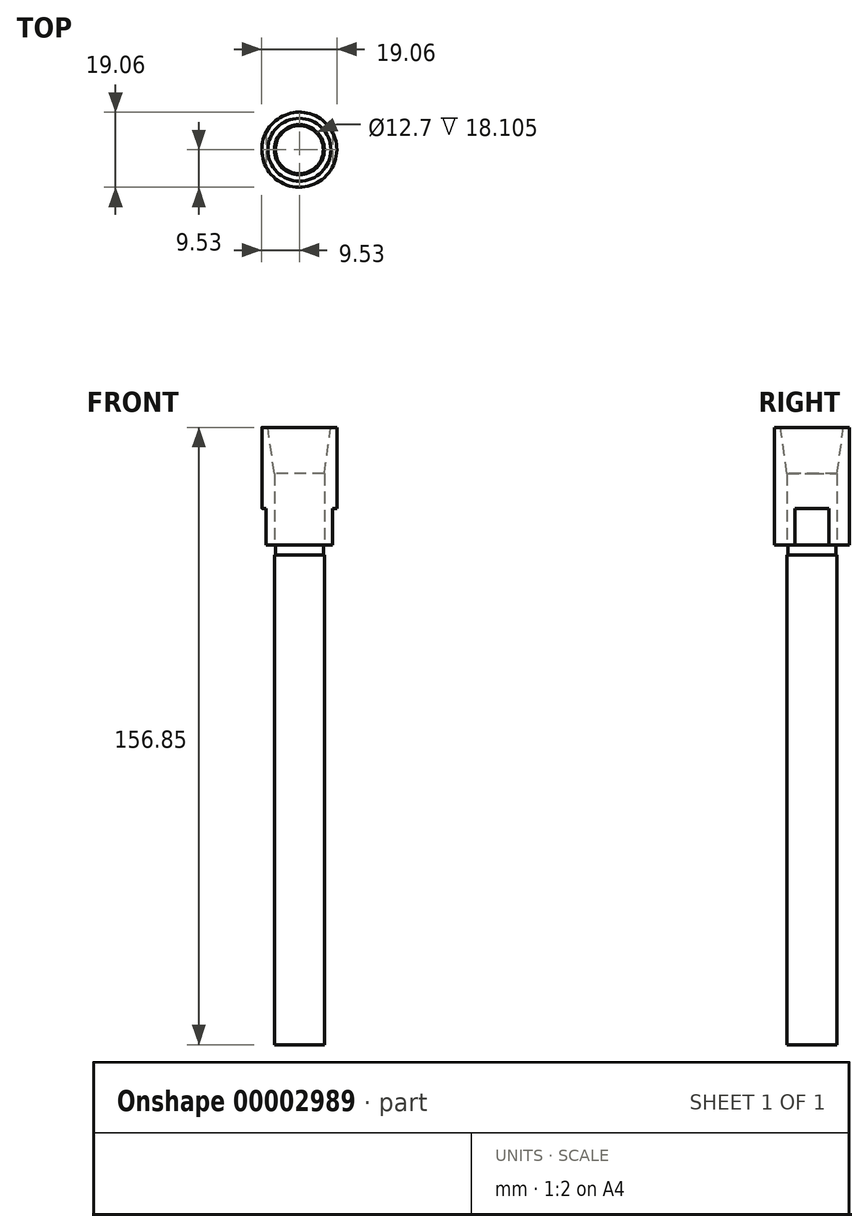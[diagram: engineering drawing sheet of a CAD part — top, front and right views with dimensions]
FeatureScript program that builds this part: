
annotation { "Feature Type Name" : "Feature", "Feature Type Description" : "" }
export const myFeature = defineFeature(function(context is Context, id is Id, definition is map)
    precondition{}
    {
        {
            var Q0;
            Q0=qCreatedBy(makeId("Top.planeOp"),FACE);
            var sketch = newSketch(context, id + "F0", { "sketchPlane" : qUnion([Q0])});
            skCircle(sketch, "E0", {"center": v(0, 0) * mm, "radius": 6.35 * mm});
            skCircle(sketch, "E1", {"center": v(0, 0) * mm, "radius": 9.53 * mm});
            skCircle(sketch, "E2", {"center": v(0, 0) * mm, "radius": 6.1 * mm});
            skSolve(sketch);
        }
        {
            var Q0;
            Q0=makeQuery(id+"F0.imprint","IMPRINT",FACE,{"disambiguationData":[TD([[makeQuery(id+"F0.imprint","IMPRINT",EDGE,{"derivedFrom":sQuery(id+"F0.wireOp",EDGE,"E0")}),1.0]])]});
            var Q1;
            Q1=makeQuery(id+"F0.imprint","IMPRINT",FACE,{"disambiguationData":[TD([[makeQuery(id+"F0.imprint","IMPRINT",EDGE,{"derivedFrom":sQuery(id+"F0.wireOp",EDGE,"E2")}),1.0]])]});
            extrude(context, id + "F1", {"entities" : qUnion([Q0, Q1]), "oppositeDirection" : true, "depth" : 127 * mm});
        }
        {
            var Q0;
            Q0=makeQuery(id+"F0.imprint","IMPRINT",FACE,{"disambiguationData":[TD([[makeQuery(id+"F0.imprint","IMPRINT",EDGE,{"derivedFrom":sQuery(id+"F0.wireOp",EDGE,"E0")}),1.0]])]});
            extrude(context, id + "F2", {"entities" : qUnion([Q0]), "operationType" : NewBodyOperationType.REMOVE, "oppositeDirection" : true, "depth" : 2.54 * mm});
        }
        {
            var Q0;
            Q0=makeQuery(id+"F0.imprint","IMPRINT",FACE,{"disambiguationData":[TD([[makeQuery(id+"F0.imprint","IMPRINT",EDGE,{"derivedFrom":sQuery(id+"F0.wireOp",EDGE,"E0")}),-1.0]])]});
            extrude(context, id + "F3", {"entities" : qUnion([Q0]), "depth" : 29.84 * mm});
        }
        {
            var Q0;
            Q0=qCreatedBy(makeId("Front.planeOp"),FACE);
            var sketch = newSketch(context, id + "F4", { "sketchPlane" : qUnion([Q0])});
            skLineSegment(sketch, "E3", {"start": v(-9.53, 0) * mm, "end": v(-9.53, 10.73) * mm, "construction": true});
            skLineSegment(sketch, "E4", {"start": v(9.53, 0) * mm, "end": v(9.53, 10.31) * mm, "construction": true});
            skLineSegment(sketch, "E5.rect.bottom", {"start": v(-10.55, 0) * mm, "end": v(-8.5, 0) * mm});
            skLineSegment(sketch, "E5.rect.top", {"start": v(-10.55, 9.27) * mm, "end": v(-8.5, 9.27) * mm});
            skLineSegment(sketch, "E5.rect.left", {"start": v(-10.55, 0) * mm, "end": v(-10.55, 9.27) * mm});
            skLineSegment(sketch, "E5.rect.right", {"start": v(-8.5, 0) * mm, "end": v(-8.5, 9.27) * mm});
            skPoint(sketch, "E5.rect.middle", {"position": v(-9.53, 4.64) * mm});
            skLineSegment(sketch, "E6", {"start": v(0, 0) * mm, "end": v(0, 9.93) * mm, "construction": true});
            skLineSegment(sketch, "E7.0.MirrorCS", {"start": v(10.55, 9.27) * mm, "end": v(8.5, 9.27) * mm});
            skLineSegment(sketch, "E8.0.MirrorCS", {"start": v(8.5, 0) * mm, "end": v(8.5, 9.27) * mm});
            skLineSegment(sketch, "E9.0.MirrorCS", {"start": v(10.55, 0) * mm, "end": v(8.5, 0) * mm});
            skLineSegment(sketch, "E10.0.MirrorCS", {"start": v(10.55, 0) * mm, "end": v(10.55, 9.27) * mm});
            skSolve(sketch);
        }
        {
            var Q0;
            Q0 = qSketchRegion(id + "F4", true);
            extrude(context, id + "F5", {"entities" : qUnion([Q0]), "operationType" : NewBodyOperationType.REMOVE, "endBound" : BoundingType.SYMMETRIC, "oppositeDirection" : true, "depth" : 25.4 * mm});
        }
        {
            var Q0;
            Q0=qCreatedBy(makeId("Right.planeOp"),FACE);
            var sketch = newSketch(context, id + "F6", { "sketchPlane" : qUnion([Q0])});
            skLineSegment(sketch, "E11.0", {"start": v(-8, 29.85) * mm, "end": v(0, 29.85) * mm});
            skLineSegment(sketch, "E12", {"start": v(-8, 29.85) * mm, "end": v(-5.58, 12.6) * mm});
            skLineSegment(sketch, "E13", {"start": v(0, 12.6) * mm, "end": v(-5.58, 12.6) * mm});
            skLineSegment(sketch, "E14", {"start": v(0, 12.6) * mm, "end": v(0, 29.85) * mm});
            skPoint(sketch, "E15.orphan", {"position": v(9.53, 29.85) * mm});
            skPoint(sketch, "E16.orphan", {"position": v(-9.53, 29.85) * mm});
            skLineSegment(sketch, "E17", {"start": v(0, 0) * mm, "end": v(0, 29.85) * mm, "construction": true});
            skSolve(sketch);
        }
        {
            var Q0;
            Q0=makeQuery(id+"F6.imprint","IMPRINT",FACE,{"disambiguationData":[TD([[makeQuery(id+"F6.imprint","IMPRINT",EDGE,{"derivedFrom":sQuery(id+"F6.wireOp",EDGE,"E11.0")}),-1.0]])]});
            var Q1;
            Q1=sQuery(id+"F6.wireOp",EDGE,"E14");
            revolve(context, id + "F7", {"operationType" : NewBodyOperationType.REMOVE, "entities" : qUnion([Q0]), "axis" : qUnion([Q1]), "revolveType" : RevolveType.FULL, "oppositeDirection" : true});
        }
    });
